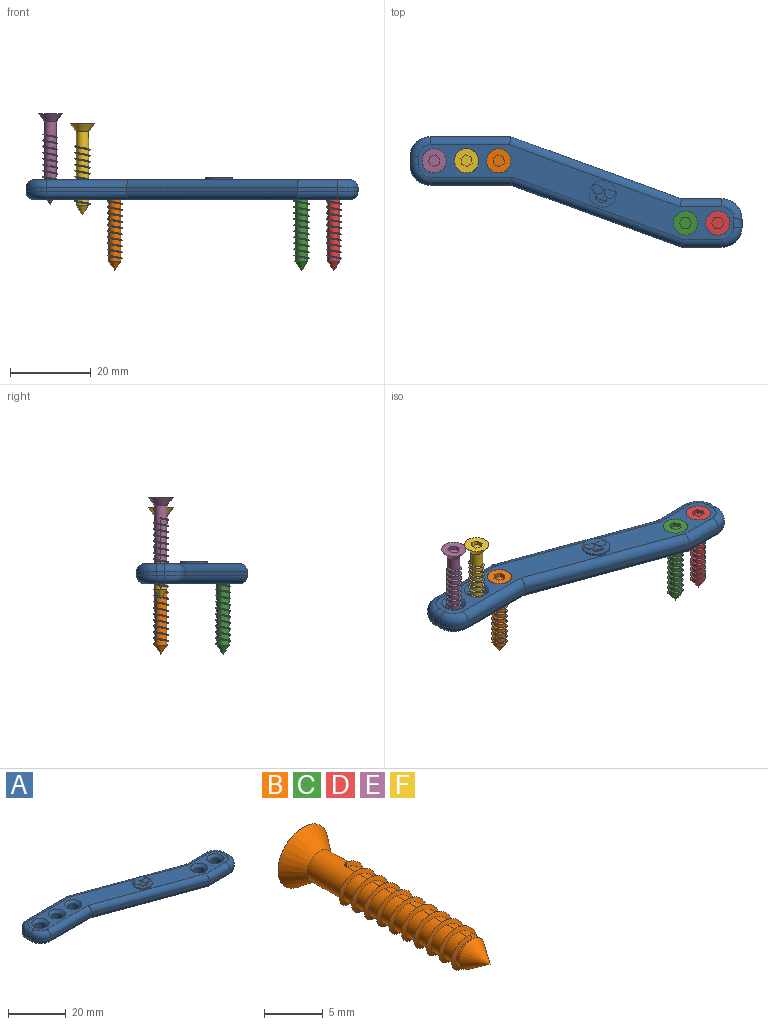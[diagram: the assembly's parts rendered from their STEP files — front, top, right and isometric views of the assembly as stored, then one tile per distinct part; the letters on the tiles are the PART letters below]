
ASSEMBLY  parts=6 mates=5
PART A: 63 faces, bbox 83.1x28.2x5.6 mm
  f0: plane 78.29x23.39mm, normal (0,0,1), area 431.1mm2, adj f23,f24,f25,f26,f27,f28,f29,f30
  f1: plane 78.29x23.39mm, normal (0,0,-1), area 544.9mm2, adj f10,f11,f12,f13,f14,f15,f16,f17
  f2: plane 20x1mm, normal (0,1,0), area 20mm2, adj f9,f16,f24,f41
  f3: plane 2x1mm, normal (-1,0,0), area 2mm2, adj f18,f26,f38,f41
  f4: plane 20x1mm, normal (0,-1,0), area 20mm2, adj f5,f20,f28,f38
  f5: plane 42.29x15.39mm, normal (-0.34,-0.94,0), area 45mm2, adj f4,f6,f22,f30
  f6: plane 10x1mm, normal (0,-1,0), area 10mm2, adj f5,f21,f29,f35
  f7: plane 2x1mm, normal (1,0,0), area 2mm2, adj f19,f27,f32,f35
  f8: plane 10x1mm, normal (0,1,0), area 10mm2, adj f9,f17,f25,f32
  f9: plane 42.29x15.39mm, normal (0.34,0.94,0), area 45mm2, adj f2,f8,f15,f23
  f10: cylinder r=2mm len=4mm, axis (0,0,1), area 50.3mm2, adj f1,f43
  f11: cylinder r=2mm len=4mm, axis (0,0,1), area 50.3mm2, adj f1,f46
  f12: cylinder r=2mm len=4mm, axis (0,0,1), area 50.3mm2, adj f1,f45
  f13: cylinder r=2mm len=4mm, axis (0,0,1), area 50.3mm2, adj f1,f44
  f14: cylinder r=2mm len=4mm, axis (0,0,1), area 50.3mm2, adj f1,f47
  f15: cylinder r=2mm len=43.3mm, axis (-0.94,0.34,0), area 141.4mm2, adj f1,f9,f16,f17
  f16: cylinder r=2mm len=20mm, axis (-1,0,0), area 62.4mm2, adj f1,f2,f15,f42
  f17: cylinder r=2mm len=10.35mm, axis (-1,0,0), area 31.8mm2, adj f1,f8,f15,f33
  f18: cylinder r=2mm len=2mm, axis (0,-1,0), area 6.3mm2, adj f1,f3,f39,f42
  f19: cylinder r=2mm len=2mm, axis (0,1,0), area 6.3mm2, adj f1,f7,f33,f36
  f20: cylinder r=2mm len=20.35mm, axis (1,0,0), area 63.2mm2, adj f1,f4,f22,f39
  f21: cylinder r=2mm len=10mm, axis (1,0,0), area 31mm2, adj f1,f6,f22,f36
  f22: cylinder r=2mm len=43.3mm, axis (0.94,-0.34,0), area 141.4mm2, adj f1,f5,f20,f21
  f23: cylinder r=2mm len=43.3mm, axis (0.94,-0.34,0), area 141.4mm2, adj f0,f9,f24,f25
  f24: cylinder r=2mm len=20mm, axis (1,0,0), area 62.4mm2, adj f0,f2,f23,f40
  f25: cylinder r=2mm len=10.35mm, axis (1,0,0), area 31.8mm2, adj f0,f8,f23,f31
  f26: cylinder r=2mm len=2mm, axis (0,1,0), area 6.3mm2, adj f0,f3,f37,f40
  f27: cylinder r=2mm len=2mm, axis (0,-1,0), area 6.3mm2, adj f0,f7,f31,f34
  f28: cylinder r=2mm len=20.35mm, axis (-1,0,0), area 63.2mm2, adj f0,f4,f30,f37
  f29: cylinder r=2mm len=10mm, axis (-1,0,0), area 31mm2, adj f0,f6,f30,f34
  f30: cylinder r=2mm len=43.3mm, axis (-0.94,0.34,0), area 141.4mm2, adj f0,f5,f28,f29
  f31: torus R=3mm, axis (0,0,1), area 21.1mm2, adj f0,f25,f27,f32
  f32: cylinder r=5mm len=5mm, axis (0,0,1), area 7.9mm2, adj f7,f8,f31,f33
  f33: torus R=3mm, axis (0,0,1), area 21.1mm2, adj f1,f17,f19,f32
  f34: torus R=3mm, axis (0,0,1), area 21.1mm2, adj f0,f27,f29,f35
  f35: cylinder r=5mm len=5mm, axis (0,0,-1), area 7.9mm2, adj f6,f7,f34,f36
  f36: torus R=3mm, axis (0,0,1), area 21.1mm2, adj f1,f19,f21,f35
  f37: torus R=3mm, axis (0,0,1), area 21.1mm2, adj f0,f26,f28,f38
  f38: cylinder r=5mm len=5mm, axis (0,0,1), area 7.9mm2, adj f3,f4,f37,f39
  f39: torus R=3mm, axis (0,0,1), area 21.1mm2, adj f1,f18,f20,f38
  f40: torus R=3mm, axis (0,0,1), area 21.1mm2, adj f0,f24,f26,f41
  f41: cylinder r=5mm len=5mm, axis (0,0,-1), area 7.9mm2, adj f2,f3,f40,f42
  f42: torus R=3mm, axis (0,0,1), area 21.1mm2, adj f1,f16,f18,f41
  f43: cone r=2mm half-angle=45deg, axis (0,0,1), area 22.2mm2, adj f0,f10
  f44: cone r=2mm half-angle=45deg, axis (0,0,1), area 22.2mm2, adj f0,f13
  f45: cone r=2mm half-angle=45deg, axis (0,0,1), area 22.2mm2, adj f0,f12
  f46: cone r=2mm half-angle=45deg, axis (0,0,1), area 22.2mm2, adj f0,f11
  f47: cone r=2mm half-angle=45deg, axis (0,0,1), area 22.2mm2, adj f0,f14
  f48: plane 5.78x3.08mm, normal (0,0,1), area 8.3mm2, adj f52,f62
  f49: plane 6.7x5.61mm, normal (0,0,1), area 16.3mm2, adj f54,f55,f60
  f50: plane 0.06x0.05mm, normal (0,0,1), area 0mm2, adj f53,f61
  f51: extruded ~0.5x0.17mm, area 0.1mm2, adj f0,f52,f54,f56
  f52: cylinder r=3.35mm len=5.77mm, axis (0,0,-1), area 3.9mm2, adj f0,f48,f51,f53
  f53: extruded ~0.5x0.06mm, area 0mm2, adj f0,f50,f52,f54
  f54: cylinder r=3.35mm len=6.7mm, axis (0,0,-1), area 6.5mm2, adj f0,f49,f51,f53
  f55: extruded ~2.89x1.6mm, area 3.7mm2, adj f49,f57
  f56: plane 0.18x0.03mm, normal (0,0,1), area 0mm2, adj f51,f59
  f57: plane 2.92x1.62mm, normal (0,0,1), area 1.5mm2, adj f55
  f58: plane 5.85x3.46mm, normal (0,0,1), area 9.2mm2, adj f59,f60,f61,f62
  f59: cylinder r=3.35mm len=0.17mm, axis (0,0,-1), area 0mm2, adj f56,f58,f60,f62
  f60: extruded ~5.83x3.37mm, area 1mm2, adj f49,f58,f59,f61
  f61: cylinder r=3.35mm len=0.1mm, axis (0,0,-1), area 0mm2, adj f50,f58,f60,f62
  f62: extruded ~5.77x2.04mm, area 0.6mm2, adj f48,f58,f59,f61
PART B: 25 faces, bbox 6x22.5x6 mm
  f0: plane 6x6mm, normal (0,1,0), area 22.4mm2, adj f12,f18,f19,f20,f21,f22,f23
  f1: cylinder r=1.5mm len=4.5mm, axis (0,1,0), area 35.3mm2, adj f2,f12,f13,f15
  f2: cylinder r=1.5mm len=3mm, axis (0,1,0), area 11.3mm2, adj f1,f3,f15,f16
  f3: cylinder r=1.5mm len=3mm, axis (0,1,0), area 11.3mm2, adj f2,f4,f15,f16
  f4: cylinder r=1.5mm len=3mm, axis (0,1,0), area 11.3mm2, adj f3,f5,f15,f16
  f5: cylinder r=1.5mm len=3mm, axis (0,1,0), area 11.3mm2, adj f4,f6,f15,f16
  f6: cylinder r=1.5mm len=3mm, axis (0,1,0), area 11.3mm2, adj f5,f7,f15,f16
  f7: cylinder r=1.5mm len=3mm, axis (0,1,0), area 11.3mm2, adj f6,f8,f15,f16
  f8: cylinder r=1.5mm len=3mm, axis (0,1,0), area 11.3mm2, adj f7,f9,f15,f16
  f9: cylinder r=1.5mm len=3mm, axis (0,1,0), area 11.3mm2, adj f8,f10,f15,f16
  f10: cylinder r=1.5mm len=3mm, axis (0,1,0), area 11.3mm2, adj f9,f11,f15,f16
  f11: cylinder r=1.5mm len=3mm, axis (0,1,0), area 7.1mm2, adj f10,f14,f16,f17
  f12: cone r=1.5mm half-angle=36.9deg, axis (0,1,0), area 35.3mm2, adj f0,f1
  f13: plane 0.4x0.3mm, normal (-1,0,0), area 0.1mm2, adj f1,f15,f16
  f14: plane 0.4x0.3mm, normal (1,0,0), area 0.1mm2, adj f11,f15,f16
  f15: bspline ~15.15x4.39mm, area 45.9mm2, adj f1,f2,f3,f4,f5,f6,f7,f8
  f16: bspline ~15.15x4.39mm, area 46mm2, adj f2,f3,f4,f5,f6,f7,f8,f9
  f17: cone r=1.5mm half-angle=34.3deg, axis (0,1,0), area 12.5mm2, adj f11
  f18: plane 1.5x1mm, normal (0,0,-1), area 1.5mm2, adj f0,f19,f23,f24
  f19: plane 1.3x1mm, normal (-0.87,0,-0.5), area 1.5mm2, adj f0,f18,f20,f24
  f20: plane 1.3x1mm, normal (-0.87,0,0.5), area 1.5mm2, adj f0,f19,f21,f24
  f21: plane 1.5x1mm, normal (0,0,1), area 1.5mm2, adj f0,f20,f22,f24
  f22: plane 1.3x1mm, normal (0.87,0,0.5), area 1.5mm2, adj f0,f21,f23,f24
  f23: plane 1.3x1mm, normal (0.87,0,-0.5), area 1.5mm2, adj f0,f18,f22,f24
  f24: plane 3x2.6mm, normal (0,1,0), area 5.8mm2, adj f18,f19,f20,f21,f22,f23
PART C: same geometry as B
PART D: same geometry as B
PART E: same geometry as B
PART F: same geometry as B
PLACE A t=(-16.84,15.58,-3.02)mm fixed
PLACE B rot(axis=(0.25,-0.69,-0.69),152.4deg) t=(5.16,21.58,2.07)mm
PLACE C rot(axis=(0.38,-0.65,-0.65),138.6deg) t=(51.44,6.19,1.98)mm
PLACE D rot(axis=(0.38,-0.65,-0.65),138.6deg) t=(59.44,6.19,1.98)mm
PLACE E rot(axis=(0.52,-0.61,-0.61),125.3deg) t=(-10.84,21.58,18.39)mm
PLACE F rot(axis=(0.14,0.7,0.7),164.2deg) t=(-2.84,21.58,15.83)mm
MATE cylindrical B.f1 <-> A.f12  axis (0,0,1) through (5.16,21.58,0.07)mm
MATE cylindrical D.f1 <-> A.f10  axis (0,0,1) through (59.44,6.19,-0.02)mm
MATE cylindrical C.f1 <-> A.f13  axis (0,0,1) through (51.44,6.19,-0.02)mm
MATE cylindrical F.f1 <-> A.f11  axis (0,0,1) through (-2.84,21.58,13.83)mm
MATE cylindrical E.f1 <-> A.f14  axis (0,0,1) through (-10.84,21.58,16.39)mm
